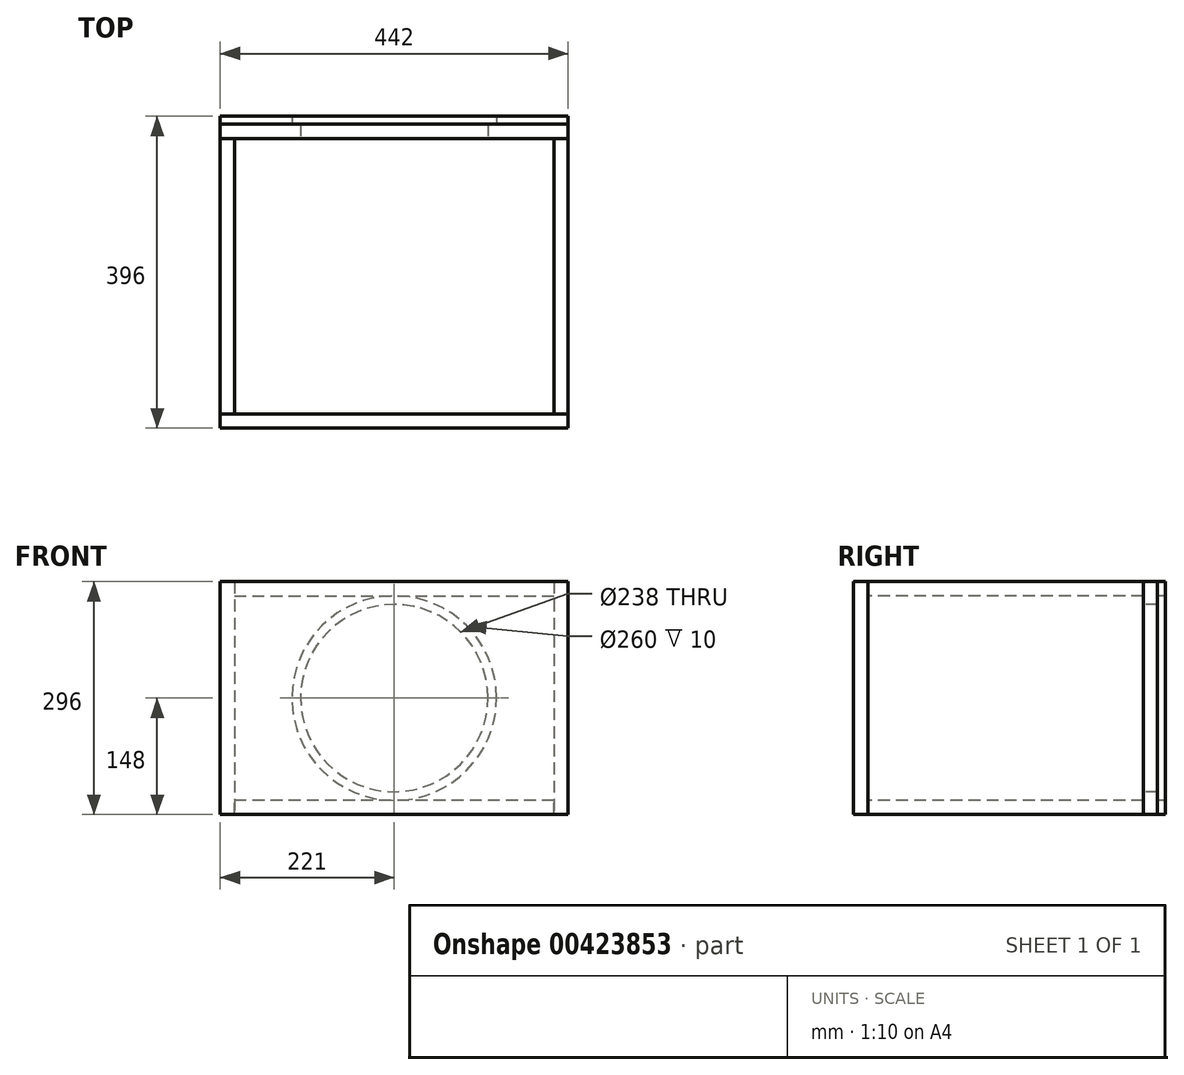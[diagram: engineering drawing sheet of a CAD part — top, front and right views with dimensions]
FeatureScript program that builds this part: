
annotation { "Feature Type Name" : "Feature", "Feature Type Description" : "" }
export const myFeature = defineFeature(function(context is Context, id is Id, definition is map)
    precondition{}
    {
        {
            var Q0;
            Q0=qCreatedBy(makeId("Front.planeOp"),FACE);
            var sketch = newSketch(context, id + "F0", { "sketchPlane" : qUnion([Q0])});
            skLineSegment(sketch, "E0.bottom", {"start": v(221, -148) * mm, "end": v(-221, -148) * mm});
            skLineSegment(sketch, "E0.top", {"start": v(221, 148) * mm, "end": v(-221, 148) * mm});
            skLineSegment(sketch, "E0.left", {"start": v(221, -148) * mm, "end": v(221, 148) * mm});
            skLineSegment(sketch, "E0.right", {"start": v(-221, -148) * mm, "end": v(-221, 148) * mm});
            skPoint(sketch, "E0.middle", {"position": v(0, 0) * mm});
            skSolve(sketch);
        }
        {
            var Q0;
            Q0=qSketchRegion(id+"F0",true);
            extrude(context, id + "F1", {"entities" : qUnion([Q0]), "depth" : 18 * mm});
        }
        {
            var Q0;
            Q0=makeQuery(id+"F1.opExtrude","CAP_FACE",FACE,{"disambiguationData":[OSD([sQuery(id+"F0.wireOp",EDGE,"E0.bottom"),sQuery(id+"F0.wireOp",EDGE,"E0.top"),sQuery(id+"F0.wireOp",EDGE,"E0.left"),sQuery(id+"F0.wireOp",EDGE,"E0.right")])],"isStart":true});
            var sketch = newSketch(context, id + "F2", { "sketchPlane" : qUnion([Q0])});
            skLineSegment(sketch, "E1.bottom", {"start": v(-221, 148) * mm, "end": v(-203, 148) * mm});
            skLineSegment(sketch, "E1.top", {"start": v(-221, -148) * mm, "end": v(-203, -148) * mm});
            skLineSegment(sketch, "E1.left", {"start": v(-221, 148) * mm, "end": v(-221, -148) * mm});
            skLineSegment(sketch, "E1.right", {"start": v(-203, 148) * mm, "end": v(-203, -148) * mm});
            skSolve(sketch);
        }
        {
            var Q0;
            Q0=qSketchRegion(id+"F2",true);
            extrude(context, id + "F3", {"entities" : qUnion([Q0]), "depth" : 350 * mm});
        }
        {
            var Q0;
            Q0=makeQuery(id+"F1.opExtrude","CAP_FACE",FACE,{"disambiguationData":[OSD([sQuery(id+"F0.wireOp",EDGE,"E0.bottom"),sQuery(id+"F0.wireOp",EDGE,"E0.top"),sQuery(id+"F0.wireOp",EDGE,"E0.left"),sQuery(id+"F0.wireOp",EDGE,"E0.right")])],"isStart":true});
            var sketch = newSketch(context, id + "F4", { "sketchPlane" : qUnion([Q0])});
            skLineSegment(sketch, "E2.bottom", {"start": v(221, 148) * mm, "end": v(203, 148) * mm});
            skLineSegment(sketch, "E2.top", {"start": v(221, -148) * mm, "end": v(203, -148) * mm});
            skLineSegment(sketch, "E2.left", {"start": v(221, 148) * mm, "end": v(221, -148) * mm});
            skLineSegment(sketch, "E2.right", {"start": v(203, 148) * mm, "end": v(203, -148) * mm});
            skSolve(sketch);
        }
        {
            var Q0;
            Q0=qSketchRegion(id+"F4",true);
            extrude(context, id + "F5", {"entities" : qUnion([Q0]), "depth" : 350 * mm});
        }
        {
            var Q0;
            Q0=makeQuery(id+"F1.opExtrude","CAP_FACE",FACE,{"disambiguationData":[OSD([sQuery(id+"F0.wireOp",EDGE,"E0.bottom"),sQuery(id+"F0.wireOp",EDGE,"E0.top"),sQuery(id+"F0.wireOp",EDGE,"E0.left"),sQuery(id+"F0.wireOp",EDGE,"E0.right")])],"isStart":true});
            var sketch = newSketch(context, id + "F6", { "sketchPlane" : qUnion([Q0])});
            skLineSegment(sketch, "E3.bottom", {"start": v(203, 148) * mm, "end": v(-203, 148) * mm});
            skLineSegment(sketch, "E3.top", {"start": v(203, 130) * mm, "end": v(-203, 130) * mm});
            skLineSegment(sketch, "E3.left", {"start": v(203, 148) * mm, "end": v(203, 130) * mm});
            skLineSegment(sketch, "E3.right", {"start": v(-203, 148) * mm, "end": v(-203, 130) * mm});
            skSolve(sketch);
        }
        {
            var Q0;
            Q0=makeQuery(id+"F6.imprint","IMPRINT",FACE,{"disambiguationData":[TD([[makeQuery(id+"F6.imprint","IMPRINT",EDGE,{"derivedFrom":sQuery(id+"F6.wireOp",EDGE,"E3.top")}),1.0]])]});
            var sketch = newSketch(context, id + "F7", { "sketchPlane" : qUnion([Q0])});
            skLineSegment(sketch, "E4.bottom", {"start": v(-203, -148) * mm, "end": v(203, -148) * mm});
            skLineSegment(sketch, "E4.top", {"start": v(-203, -130) * mm, "end": v(203, -130) * mm});
            skLineSegment(sketch, "E4.left", {"start": v(-203, -148) * mm, "end": v(-203, -130) * mm});
            skLineSegment(sketch, "E4.right", {"start": v(203, -148) * mm, "end": v(203, -130) * mm});
            skSolve(sketch);
        }
        {
            var Q0;
            Q0=qSketchRegion(id+"F6",true);
            extrude(context, id + "F8", {"entities" : qUnion([Q0]), "depth" : 350 * mm});
        }
        {
            var Q0;
            Q0=qSketchRegion(id+"F7",true);
            extrude(context, id + "F9", {"entities" : qUnion([Q0]), "depth" : 350 * mm});
        }
        {
            var Q0;
            Q0=makeQuery(id+"F8.opExtrude","CAP_FACE",FACE,{"disambiguationData":[OSD([sQuery(id+"F6.wireOp",EDGE,"E3.bottom"),sQuery(id+"F6.wireOp",EDGE,"E3.top"),sQuery(id+"F6.wireOp",EDGE,"E3.left"),sQuery(id+"F6.wireOp",EDGE,"E3.right")])],"isStart":false});
            var sketch = newSketch(context, id + "F10", { "sketchPlane" : qUnion([Q0])});
            skLineSegment(sketch, "E5.bottom", {"start": v(-221, 148) * mm, "end": v(221, 148) * mm});
            skLineSegment(sketch, "E5.top", {"start": v(-221, -148) * mm, "end": v(221, -148) * mm});
            skLineSegment(sketch, "E5.left", {"start": v(-221, 148) * mm, "end": v(-221, -148) * mm});
            skLineSegment(sketch, "E5.right", {"start": v(221, 148) * mm, "end": v(221, -148) * mm});
            skCircle(sketch, "E6", {"center": v(0, 0) * mm, "radius": 119 * mm});
            skSolve(sketch);
        }
        {
            var Q0;
            Q0=qSketchRegion(id+"F10",true);
            extrude(context, id + "F11", {"entities" : qUnion([Q0]), "depth" : 18 * mm});
        }
        {
            var Q0;
            Q0=makeQuery(id+"F11.opExtrude","SWEPT_BODY",BODY,{"disambiguationData":[OSD([sQuery(id+"F10.wireOp",EDGE,"E5.bottom"),sQuery(id+"F10.wireOp",EDGE,"E5.top"),sQuery(id+"F10.wireOp",EDGE,"E5.left"),sQuery(id+"F10.wireOp",EDGE,"E5.right"),sQuery(id+"F10.wireOp",EDGE,"E6")])]});
            transform(context, id + "F12", {"entities" : qUnion([Q0]), "transformType" : TransformType.TRANSLATION_3D, "dx" : 0 * mm, "dy" : 18 * mm, "dz" : 0 * mm, "makeCopy" : true});
        }
        {
            var Q0;
            Q0=makeQuery(id+"F12.opPattern","COPY",BODY,{"derivedFrom":makeQuery(id+"F11.opExtrude","SWEPT_BODY",BODY,{"disambiguationData":[OSD([sQuery(id+"F10.wireOp",EDGE,"E5.bottom"),sQuery(id+"F10.wireOp",EDGE,"E5.top"),sQuery(id+"F10.wireOp",EDGE,"E5.left"),sQuery(id+"F10.wireOp",EDGE,"E5.right"),sQuery(id+"F10.wireOp",EDGE,"E6")])]}),"instanceName":"1"});
            deleteBodies(context, id + "F13", {"entities" : qUnion([Q0])});
        }
        {
            var Q0;
            Q0=makeQuery(id+"F11.opExtrude","CAP_FACE",FACE,{"disambiguationData":[OSD([sQuery(id+"F10.wireOp",EDGE,"E5.bottom"),sQuery(id+"F10.wireOp",EDGE,"E5.top"),sQuery(id+"F10.wireOp",EDGE,"E5.left"),sQuery(id+"F10.wireOp",EDGE,"E5.right"),sQuery(id+"F10.wireOp",EDGE,"E6")])],"isStart":false});
            var sketch = newSketch(context, id + "F14", { "sketchPlane" : qUnion([Q0])});
            skLineSegment(sketch, "E7.bottom", {"start": v(-221, 148) * mm, "end": v(221, 148) * mm});
            skLineSegment(sketch, "E7.top", {"start": v(-221, -148) * mm, "end": v(221, -148) * mm});
            skLineSegment(sketch, "E7.left", {"start": v(-221, 148) * mm, "end": v(-221, -148) * mm});
            skLineSegment(sketch, "E7.right", {"start": v(221, 148) * mm, "end": v(221, -148) * mm});
            skCircle(sketch, "E8", {"center": v(0, 0) * mm, "radius": 130 * mm});
            skSolve(sketch);
        }
        {
            var Q0;
            Q0=qSketchRegion(id+"F14",true);
            extrude(context, id + "F15", {"entities" : qUnion([Q0]), "depth" : 10 * mm});
        }
    });
